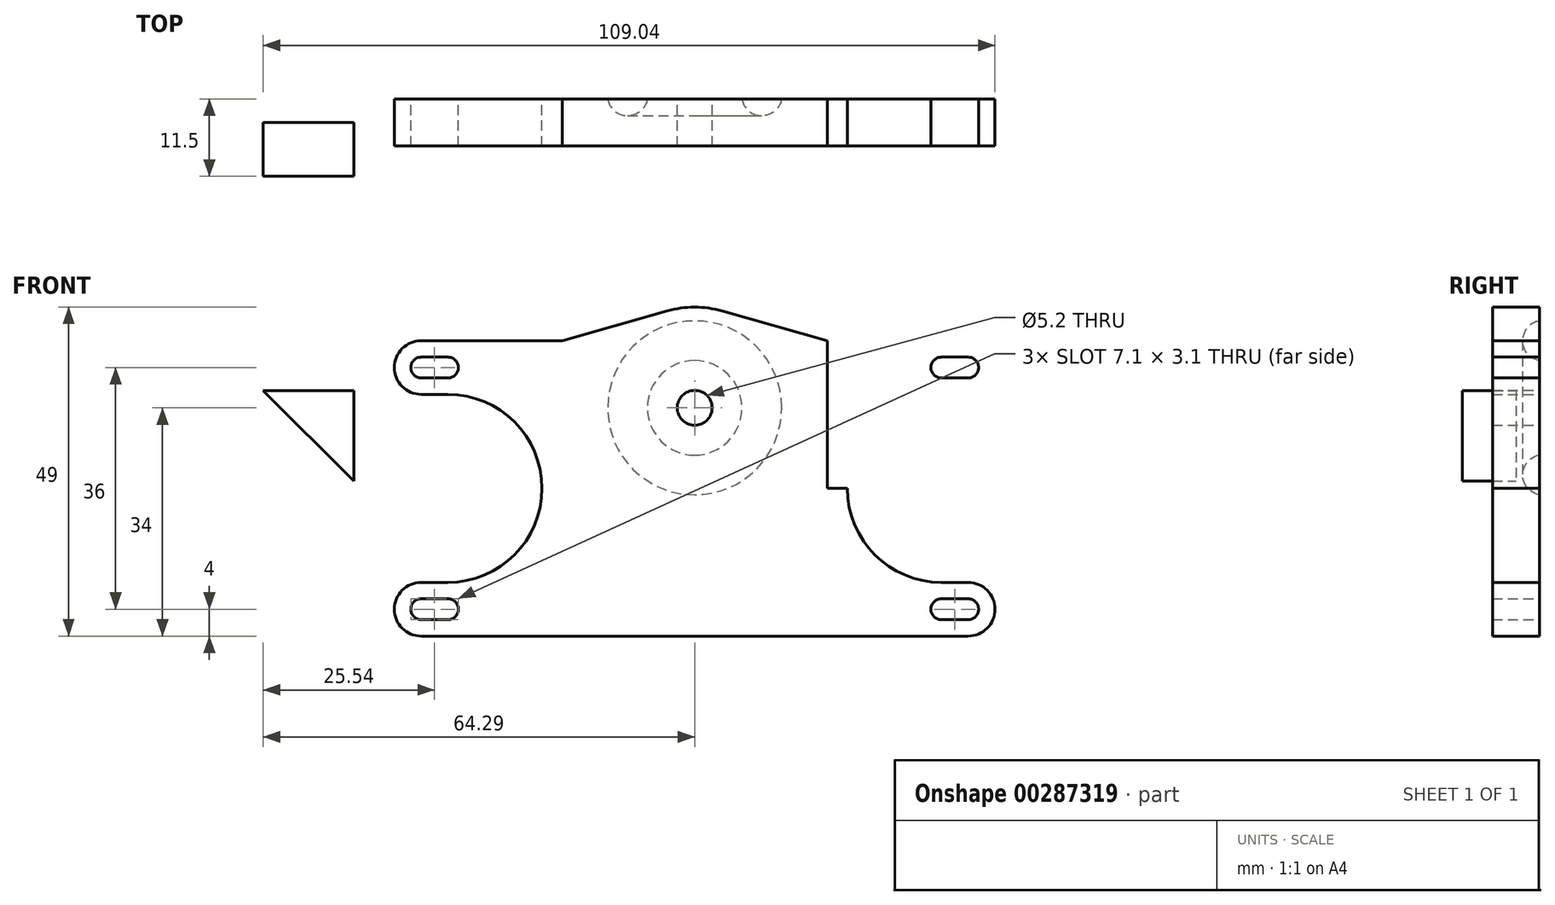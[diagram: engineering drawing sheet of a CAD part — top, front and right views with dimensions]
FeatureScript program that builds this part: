
annotation { "Feature Type Name" : "Feature", "Feature Type Description" : "" }
export const myFeature = defineFeature(function(context is Context, id is Id, definition is map)
    precondition{}
    {
        {
            var Q0;
            Q0=qCreatedBy(makeId("Front.planeOp"),FACE);
            var sketch = newSketch(context, id + "F0", { "sketchPlane" : qUnion([Q0])});
            skCircle(sketch, "E0", {"center": v(0, -2.58) * mm, "radius": 2.6 * mm});
            skCircle(sketch, "E1", {"center": v(0, -2.58) * mm, "radius": 15 * mm});
            skLineSegment(sketch, "E2", {"start": v(-35.52, 7.42) * mm, "end": v(-35.52, 7.42) * mm});
            skArc(sketch, "E3.trimOffspring", {"start": v(-40.75, 7.42) * mm, "mid": v(-44.75, 3.42) * mm, "end": v(-40.75, -0.58) * mm});
            skArc(sketch, "E4", {"start": v(-36.75, 1.87) * mm, "mid": v(-35.2, 3.42) * mm, "end": v(-36.75, 4.97) * mm});
            skLineSegment(sketch, "E5", {"start": v(-40.75, 4.97) * mm, "end": v(-36.75, 4.97) * mm});
            skLineSegment(sketch, "E6", {"start": v(-40.75, 7.42) * mm, "end": v(-19.75, 7.42) * mm});
            skLineSegment(sketch, "E7", {"start": v(-19.75, 7.42) * mm, "end": v(-4.08, 11.85) * mm});
            skLineSegment(sketch, "E8", {"start": v(-36.75, 1.87) * mm, "end": v(-40.75, 1.87) * mm});
            skArc(sketch, "E9", {"start": v(-40.75, 4.97) * mm, "mid": v(-42.3, 3.42) * mm, "end": v(-40.75, 1.87) * mm});
            skLineSegment(sketch, "E10", {"start": v(-50.79, 0) * mm, "end": v(-50.79, -13.5) * mm});
            skLineSegment(sketch, "E11", {"start": v(-50.79, 0) * mm, "end": v(-64.29, 0) * mm});
            skLineSegment(sketch, "E12", {"start": v(-64.29, 0) * mm, "end": v(-50.79, -13.5) * mm});
            skLineSegment(sketch, "E13.MirrorCS", {"start": v(-22.75, -14.58) * mm, "end": v(-19.75, -14.58) * mm});
            skLineSegment(sketch, "E14", {"start": v(-19.75, -14.58) * mm, "end": v(-19.75, 7.42) * mm});
            skLineSegment(sketch, "E15.MirrorCS", {"start": v(-19.75, -14.58) * mm, "end": v(-19.75, -36.58) * mm});
            skArc(sketch, "E16.MirrorCS", {"start": v(-40.75, -34.13) * mm, "mid": v(-42.3, -32.58) * mm, "end": v(-40.75, -31.03) * mm});
            skLineSegment(sketch, "E17.MirrorCS", {"start": v(-40.75, -34.13) * mm, "end": v(-36.75, -34.13) * mm});
            skArc(sketch, "E18.MirrorCS", {"start": v(-36.75, -31.03) * mm, "mid": v(-35.2, -32.58) * mm, "end": v(-36.75, -34.13) * mm});
            skLineSegment(sketch, "E19.MirrorCS", {"start": v(-36.75, -31.03) * mm, "end": v(-40.75, -31.03) * mm});
            skArc(sketch, "E20.MirrorCS", {"start": v(-40.75, -36.58) * mm, "mid": v(-44.75, -32.58) * mm, "end": v(-40.75, -28.58) * mm});
            skLineSegment(sketch, "E21.MirrorCS", {"start": v(-40.75, -36.58) * mm, "end": v(-19.75, -36.58) * mm});
            skLineSegment(sketch, "E22", {"start": v(-19.75, -36.58) * mm, "end": v(0, -36.58) * mm});
            skLineSegment(sketch, "E23", {"start": v(-40.75, -0.58) * mm, "end": v(-36.75, -0.58) * mm});
            skLineSegment(sketch, "E24.MirrorCS", {"start": v(-40.75, -28.58) * mm, "end": v(-36.75, -28.58) * mm});
            skArc(sketch, "E25", {"start": v(-36.75, -28.58) * mm, "mid": v(-22.75, -14.58) * mm, "end": v(-36.75, -0.58) * mm});
            skLineSegment(sketch, "E26.MirrorCS", {"start": v(19.75, -36.58) * mm, "end": v(0, -36.58) * mm});
            skArc(sketch, "E27.MirrorCS", {"start": v(36.75, 1.87) * mm, "mid": v(35.2, 3.42) * mm, "end": v(36.75, 4.97) * mm});
            skLineSegment(sketch, "E28.MirrorCS", {"start": v(40.75, 4.97) * mm, "end": v(36.75, 4.97) * mm});
            skArc(sketch, "E29.MirrorCS", {"start": v(40.75, -34.13) * mm, "mid": v(42.3, -32.58) * mm, "end": v(40.75, -31.03) * mm});
            skArc(sketch, "E30.MirrorCS", {"start": v(36.75, -31.03) * mm, "mid": v(35.2, -32.58) * mm, "end": v(36.75, -34.13) * mm});
            skLineSegment(sketch, "E31.MirrorCS", {"start": v(40.75, -34.13) * mm, "end": v(36.75, -34.13) * mm});
            skLineSegment(sketch, "E32.MirrorCS", {"start": v(22.75, -14.58) * mm, "end": v(19.75, -14.58) * mm});
            skLineSegment(sketch, "E33.MirrorCS", {"start": v(36.75, 1.87) * mm, "end": v(40.75, 1.87) * mm});
            skLineSegment(sketch, "E34.MirrorCS", {"start": v(19.75, 7.42) * mm, "end": v(4.08, 11.85) * mm});
            skLineSegment(sketch, "E35.MirrorCS", {"start": v(40.75, -0.58) * mm, "end": v(36.75, -0.58) * mm});
            skLineSegment(sketch, "E36.MirrorCS", {"start": v(36.75, -31.03) * mm, "end": v(40.75, -31.03) * mm});
            skLineSegment(sketch, "E37.MirrorCS", {"start": v(40.75, -28.58) * mm, "end": v(36.75, -28.58) * mm});
            skLineSegment(sketch, "E38.MirrorCS", {"start": v(19.75, -14.58) * mm, "end": v(19.75, -36.58) * mm});
            skLineSegment(sketch, "E39.MirrorCS", {"start": v(19.75, -14.58) * mm, "end": v(19.75, 7.42) * mm});
            skArc(sketch, "E40.MirrorCS", {"start": v(36.75, -28.58) * mm, "mid": v(22.75, -14.58) * mm, "end": v(36.75, -0.58) * mm});
            skLineSegment(sketch, "E41.MirrorCS", {"start": v(40.75, -36.58) * mm, "end": v(19.75, -36.58) * mm});
            skArc(sketch, "E42.MirrorCS", {"start": v(40.75, -36.58) * mm, "mid": v(44.75, -32.58) * mm, "end": v(40.75, -28.58) * mm});
            skLineSegment(sketch, "E43.MirrorCS", {"start": v(40.75, 7.42) * mm, "end": v(19.75, 7.42) * mm});
            skArc(sketch, "E44.MirrorCS", {"start": v(40.75, 7.42) * mm, "mid": v(44.75, 3.42) * mm, "end": v(40.75, -0.58) * mm});
            skArc(sketch, "E45.MirrorCS", {"start": v(40.75, 4.97) * mm, "mid": v(42.3, 3.42) * mm, "end": v(40.75, 1.87) * mm});
            skSolve(sketch);
        }
        {
            var Q0;
            Q0=makeQuery(id+"F0.imprint","IMPRINT",FACE,{"disambiguationData":[TD([[makeQuery(id+"F0.imprint","IMPRINT",EDGE,{"derivedFrom":sQuery(id+"F0.wireOp",EDGE,"E27.MirrorCS")}),1.0]])]});
            var Q1;
            Q1=makeQuery(id+"F0.imprint","IMPRINT",FACE,{"disambiguationData":[TD([[makeQuery(id+"F0.imprint","IMPRINT",EDGE,{"derivedFrom":sQuery(id+"F0.wireOp",EDGE,"E29.MirrorCS")}),-1.0]])]});
            var Q2;
            {var subQ0=sQuery(id+"F0.wireOp",EDGE,"E7");Q2=makeQuery(id+"F0.imprint","IMPRINT",FACE,{"disambiguationData":[TD([[makeQuery(id+"F0.imprint","IMPRINT",EDGE,{"derivedFrom":subQ0}),-1.0]])]});}
            var Q3;
            Q3=makeQuery(id+"F0.imprint","IMPRINT",FACE,{"disambiguationData":[TD([[makeQuery(id+"F0.imprint","IMPRINT",EDGE,{"derivedFrom":sQuery(id+"F0.wireOp",EDGE,"E0")}),-1.0]])]});
            var Q4;
            Q4=makeQuery(id+"F0.imprint","IMPRINT",FACE,{"disambiguationData":[TD([[makeQuery(id+"F0.imprint","IMPRINT",EDGE,{"derivedFrom":sQuery(id+"F0.wireOp",EDGE,"E3.trimOffspring")}),1.0]])]});
            var Q5;
            {var subQ0=sQuery(id+"F0.wireOp",EDGE,"E13.MirrorCS");Q5=makeQuery(id+"F0.imprint","IMPRINT",FACE,{"disambiguationData":[TD([[makeQuery(id+"F0.imprint","IMPRINT",EDGE,{"derivedFrom":subQ0}),-1.0]])]});}
            extrude(context, id + "F1", {"entities" : qUnion([Q0, Q1, Q2, Q3, Q4, Q5]), "depth" : 3.5 * mm, "hasSecondDirection" : true, "secondDirectionOppositeDirection" : true, "secondDirectionDepth" : 3.5 * mm});
        }
        {
            var Q0;
            Q0=makeQuery(id+"F0.imprint","IMPRINT",FACE,{"disambiguationData":[TD([[makeQuery(id+"F0.imprint","IMPRINT",EDGE,{"derivedFrom":sQuery(id+"F0.wireOp",EDGE,"E10")}),-1.0]])]});
            extrude(context, id + "F2", {"entities" : qUnion([Q0]), "depth" : 8 * mm});
        }
        {
            var Q0;
            Q0=qCreatedBy(makeId("Right.planeOp"),FACE);
            var sketch = newSketch(context, id + "F3", { "sketchPlane" : qUnion([Q0])});
            skCircle(sketch, "E46", {"center": v(4, 7.42) * mm, "radius": 3 * mm});
            skSolve(sketch);
        }
        {
            var Q0;
            Q0=makeQuery(id+"F3.imprint","IMPRINT",FACE,{"disambiguationData":[TD([[makeQuery(id+"F3.imprint","IMPRINT",EDGE,{"derivedFrom":sQuery(id+"F3.wireOp",EDGE,"E46")}),1.0]])]});
            var Q1;
            Q1=sQuery(id+"F0.wireOp",EDGE,"E1");
            revolve(context, id + "F4", {"operationType" : NewBodyOperationType.REMOVE, "entities" : qUnion([Q0]), "axis" : qUnion([Q1]), "revolveType" : RevolveType.FULL, "oppositeDirection" : true});
        }
    });
